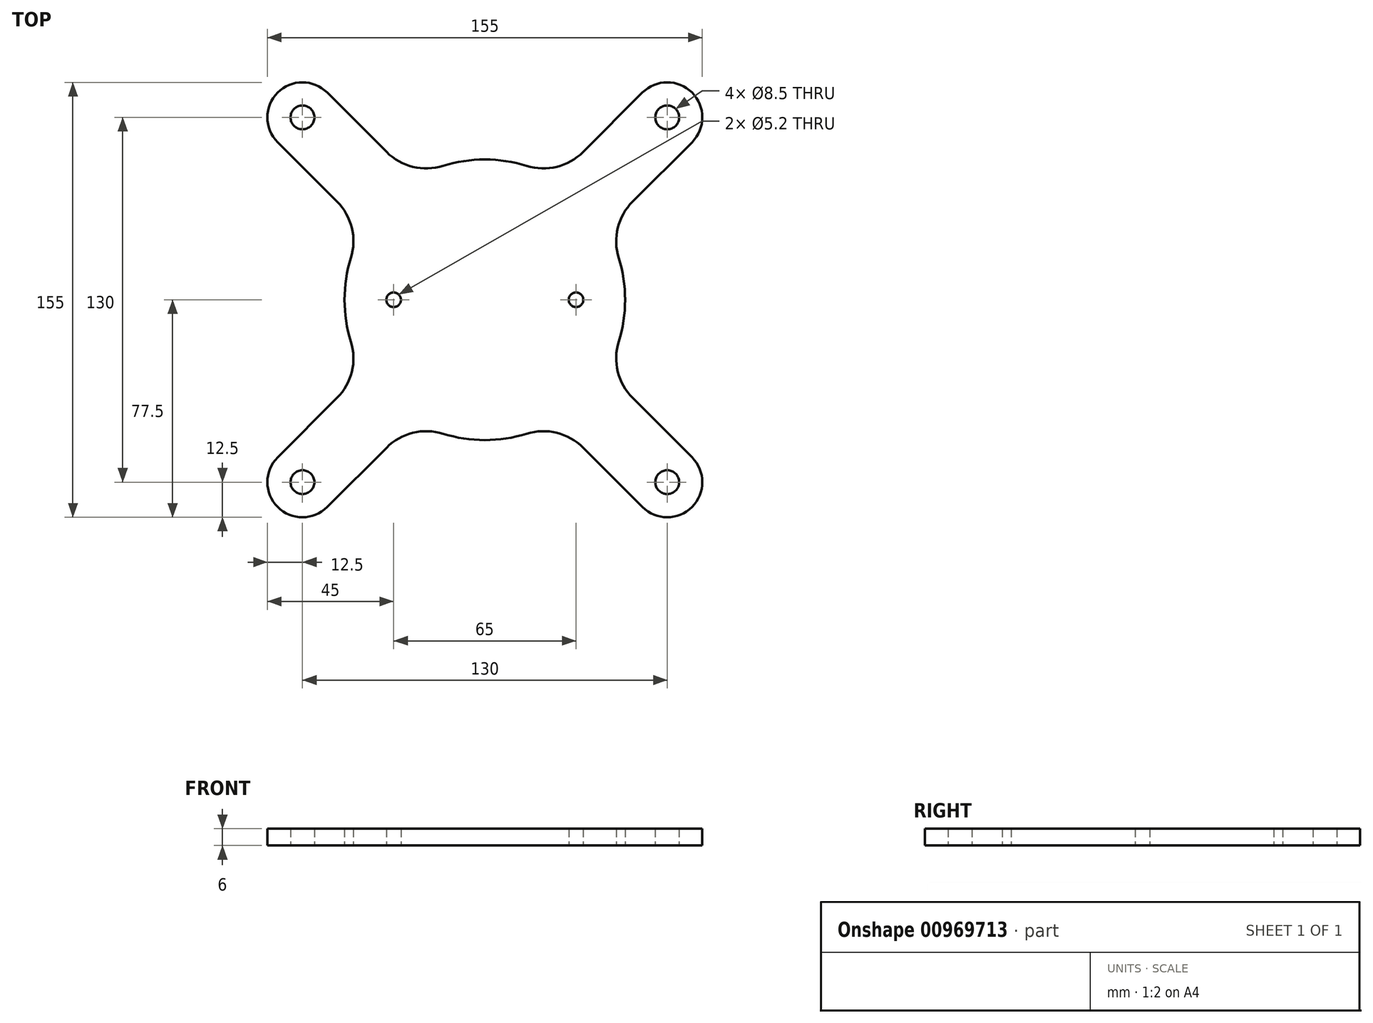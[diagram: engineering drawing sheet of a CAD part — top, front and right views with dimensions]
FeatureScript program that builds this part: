
annotation { "Feature Type Name" : "Feature", "Feature Type Description" : "" }
export const myFeature = defineFeature(function(context is Context, id is Id, definition is map)
    precondition{}
    {
        {
            var Q0;
            Q0=qCreatedBy(makeId("Top.planeOp"),FACE);
            var sketch = newSketch(context, id + "F0", { "sketchPlane" : qUnion([Q0])});
            skArc(sketch, "E0", {"start": v(25.4, 43.07) * mm, "mid": v(0, 50) * mm, "end": v(-25.4, 43.07) * mm});
            skCircle(sketch, "E1", {"center": v(-32.5, 0) * mm, "radius": 2.6 * mm});
            skCircle(sketch, "E2.MirrorC", {"center": v(32.5, 0) * mm, "radius": 2.6 * mm});
            skCircle(sketch, "E3", {"center": v(65, 65) * mm, "radius": 4.25 * mm});
            skArc(sketch, "E4", {"start": v(73.84, 56.16) * mm, "mid": v(73.84, 73.84) * mm, "end": v(56.16, 73.84) * mm});
            skLineSegment(sketch, "E5", {"start": v(25.4, 43.07) * mm, "end": v(56.16, 73.84) * mm});
            skLineSegment(sketch, "E6", {"start": v(43.07, 25.4) * mm, "end": v(73.84, 56.16) * mm});
            skCircle(sketch, "E7.1.0", {"center": v(-65, 65) * mm, "radius": 4.25 * mm});
            skArc(sketch, "E7.1.1", {"start": v(-56.16, 73.84) * mm, "mid": v(-73.84, 73.84) * mm, "end": v(-73.84, 56.16) * mm});
            skLineSegment(sketch, "E7.1.2", {"start": v(-43.07, 25.4) * mm, "end": v(-73.84, 56.16) * mm});
            skLineSegment(sketch, "E7.1.3", {"start": v(-25.4, 43.07) * mm, "end": v(-56.16, 73.84) * mm});
            skCircle(sketch, "E7.2.0", {"center": v(-65, -65) * mm, "radius": 4.25 * mm});
            skArc(sketch, "E7.2.1", {"start": v(-73.84, -56.16) * mm, "mid": v(-73.84, -73.84) * mm, "end": v(-56.16, -73.84) * mm});
            skLineSegment(sketch, "E7.2.2", {"start": v(-25.4, -43.07) * mm, "end": v(-56.16, -73.84) * mm});
            skLineSegment(sketch, "E7.2.3", {"start": v(-43.07, -25.4) * mm, "end": v(-73.84, -56.16) * mm});
            skCircle(sketch, "E7.3.0", {"center": v(65, -65) * mm, "radius": 4.25 * mm});
            skArc(sketch, "E7.3.1", {"start": v(56.16, -73.84) * mm, "mid": v(73.84, -73.84) * mm, "end": v(73.84, -56.16) * mm});
            skLineSegment(sketch, "E7.3.2", {"start": v(43.07, -25.4) * mm, "end": v(73.84, -56.16) * mm});
            skLineSegment(sketch, "E7.3.3", {"start": v(25.4, -43.07) * mm, "end": v(56.16, -73.84) * mm});
            skArc(sketch, "E8.trimOffspring", {"start": v(-43.07, 25.4) * mm, "mid": v(-50, 0) * mm, "end": v(-43.07, -25.4) * mm});
            skArc(sketch, "E9.trimOffspring", {"start": v(-25.4, -43.07) * mm, "mid": v(0, -50) * mm, "end": v(25.4, -43.07) * mm});
            skArc(sketch, "E10.trimOffspring", {"start": v(43.07, -25.4) * mm, "mid": v(50, 0) * mm, "end": v(43.07, 25.4) * mm});
            skSolve(sketch);
        }
        {
            var Q0;
            Q0=makeQuery(id+"F0.imprint","IMPRINT",FACE,{"disambiguationData":[TD([[makeQuery(id+"F0.imprint","IMPRINT",EDGE,{"derivedFrom":sQuery(id+"F0.wireOp",EDGE,"E0")}),1.0]])]});
            extrude(context, id + "F1", {"entities" : qUnion([Q0]), "depth" : 6 * mm, "offsetDistance" : 25 * mm});
        }
        {
            var Q0;
            Q0=makeQuery(id+"F1.opExtrude","SWEPT_EDGE",EDGE,{"disambiguationData":[OSD([sQuery(id+"F0.wireOp",EDGE,"E7.2.2"),sQuery(id+"F0.wireOp",EDGE,"E9.trimOffspring")])]});
            var Q1;
            Q1=makeQuery(id+"F1.opExtrude","SWEPT_EDGE",EDGE,{"disambiguationData":[OSD([sQuery(id+"F0.wireOp",EDGE,"E7.3.3"),sQuery(id+"F0.wireOp",EDGE,"E9.trimOffspring")])]});
            var Q2;
            Q2=makeQuery(id+"F1.opExtrude","SWEPT_EDGE",EDGE,{"disambiguationData":[OSD([sQuery(id+"F0.wireOp",EDGE,"E7.3.2"),sQuery(id+"F0.wireOp",EDGE,"E10.trimOffspring")])]});
            var Q3;
            Q3=makeQuery(id+"F1.opExtrude","SWEPT_EDGE",EDGE,{"disambiguationData":[OSD([sQuery(id+"F0.wireOp",EDGE,"E6"),sQuery(id+"F0.wireOp",EDGE,"E10.trimOffspring")])]});
            var Q4;
            Q4=makeQuery(id+"F1.opExtrude","SWEPT_EDGE",EDGE,{"disambiguationData":[OSD([sQuery(id+"F0.wireOp",EDGE,"E0"),sQuery(id+"F0.wireOp",EDGE,"E5")])]});
            var Q5;
            Q5=makeQuery(id+"F1.opExtrude","SWEPT_EDGE",EDGE,{"disambiguationData":[OSD([sQuery(id+"F0.wireOp",EDGE,"E0"),sQuery(id+"F0.wireOp",EDGE,"E7.1.3")])]});
            var Q6;
            Q6=makeQuery(id+"F1.opExtrude","SWEPT_EDGE",EDGE,{"disambiguationData":[OSD([sQuery(id+"F0.wireOp",EDGE,"E7.1.2"),sQuery(id+"F0.wireOp",EDGE,"E8.trimOffspring")])]});
            var Q7;
            Q7=makeQuery(id+"F1.opExtrude","SWEPT_EDGE",EDGE,{"disambiguationData":[OSD([sQuery(id+"F0.wireOp",EDGE,"E7.2.3"),sQuery(id+"F0.wireOp",EDGE,"E8.trimOffspring")])]});
            fillet(context, id + "F2", {"entities" : qUnion([Q0, Q1, Q2, Q3, Q4, Q5, Q6, Q7]), "radius" : 20 * mm, "tangentPropagation" : true, "allowEdgeOverflow" : false});
        }
    });
